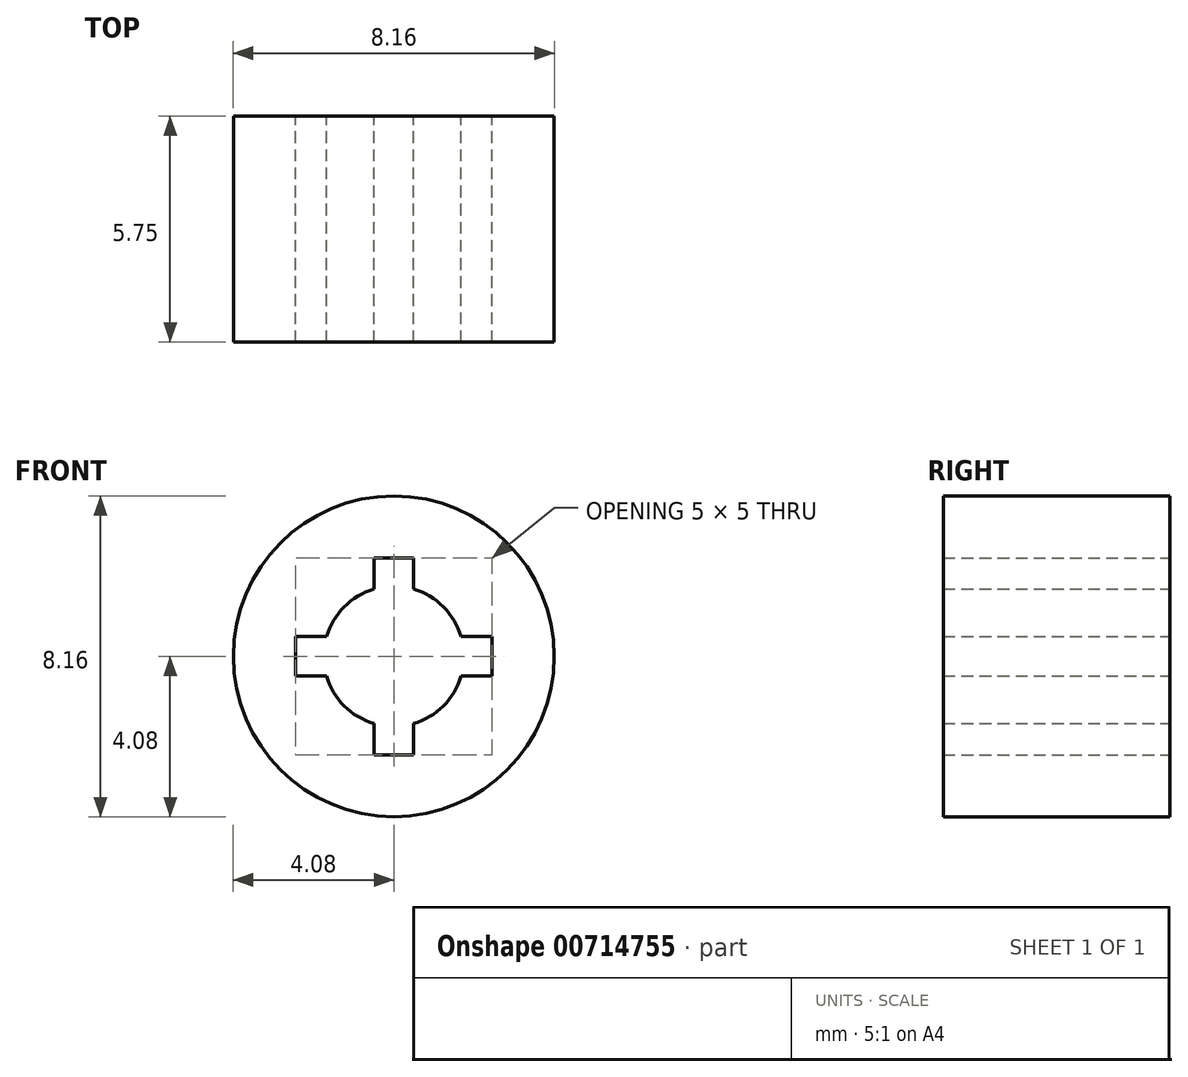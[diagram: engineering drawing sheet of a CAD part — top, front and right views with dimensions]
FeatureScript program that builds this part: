
annotation { "Feature Type Name" : "Feature", "Feature Type Description" : "" }
export const myFeature = defineFeature(function(context is Context, id is Id, definition is map)
    precondition{}
    {
        {
            var Q0;
            Q0=qCreatedBy(makeId("Front.planeOp"),FACE);
            var sketch = newSketch(context, id + "F0", { "sketchPlane" : qUnion([Q0])});
            skCircle(sketch, "E0", {"center": v(0, 0) * mm, "radius": 4.08 * mm});
            skLineSegment(sketch, "E1", {"start": v(0.5, 2.5) * mm, "end": v(-0.5, 2.5) * mm});
            skLineSegment(sketch, "E2", {"start": v(0.5, -2.5) * mm, "end": v(-0.5, -2.5) * mm});
            skLineSegment(sketch, "E3", {"start": v(-2.5, 0.5) * mm, "end": v(-2.5, -0.5) * mm});
            skLineSegment(sketch, "E4", {"start": v(2.5, 0.5) * mm, "end": v(2.5, -0.5) * mm});
            skArc(sketch, "E5", {"start": v(-0.5, 1.7) * mm, "mid": v(-1.26, 1.26) * mm, "end": v(-1.7, 0.5) * mm});
            skLineSegment(sketch, "E6", {"start": v(-0.5, 2.5) * mm, "end": v(-0.5, 1.7) * mm});
            skLineSegment(sketch, "E7", {"start": v(0.5, 2.5) * mm, "end": v(0.5, 1.7) * mm});
            skLineSegment(sketch, "E8", {"start": v(-2.5, 0.5) * mm, "end": v(-1.7, 0.5) * mm});
            skLineSegment(sketch, "E9", {"start": v(-2.5, -0.5) * mm, "end": v(-1.7, -0.5) * mm});
            skLineSegment(sketch, "E10", {"start": v(2.5, 0.5) * mm, "end": v(1.7, 0.5) * mm});
            skLineSegment(sketch, "E11", {"start": v(2.5, -0.5) * mm, "end": v(1.7, -0.5) * mm});
            skLineSegment(sketch, "E12", {"start": v(-0.5, -2.5) * mm, "end": v(-0.5, -1.7) * mm});
            skLineSegment(sketch, "E13", {"start": v(0.5, -2.5) * mm, "end": v(0.5, -1.7) * mm});
            skArc(sketch, "E14.trimOffspring", {"start": v(-1.7, -0.5) * mm, "mid": v(-1.26, -1.26) * mm, "end": v(-0.5, -1.7) * mm});
            skArc(sketch, "E15.trimOffspring", {"start": v(1.7, 0.5) * mm, "mid": v(1.26, 1.26) * mm, "end": v(0.5, 1.7) * mm});
            skArc(sketch, "E16.trimOffspring", {"start": v(0.5, -1.7) * mm, "mid": v(1.26, -1.26) * mm, "end": v(1.7, -0.5) * mm});
            skPoint(sketch, "E17.start.orphan", {"position": v(-4.08, 0) * mm});
            skPoint(sketch, "E18.start.orphan", {"position": v(0, 4.08) * mm});
            skPoint(sketch, "E19.start.orphan", {"position": v(0, -4.08) * mm});
            skPoint(sketch, "E20.start.orphan", {"position": v(4.08, 0) * mm});
            skSolve(sketch);
        }
        {
            var Q0;
            Q0 = qSketchRegion(id + "F0", true);
            extrude(context, id + "F1", {"entities" : qUnion([Q0]), "depth" : 5.75 * mm, "offsetDistance" : 25 * mm});
        }
    });
